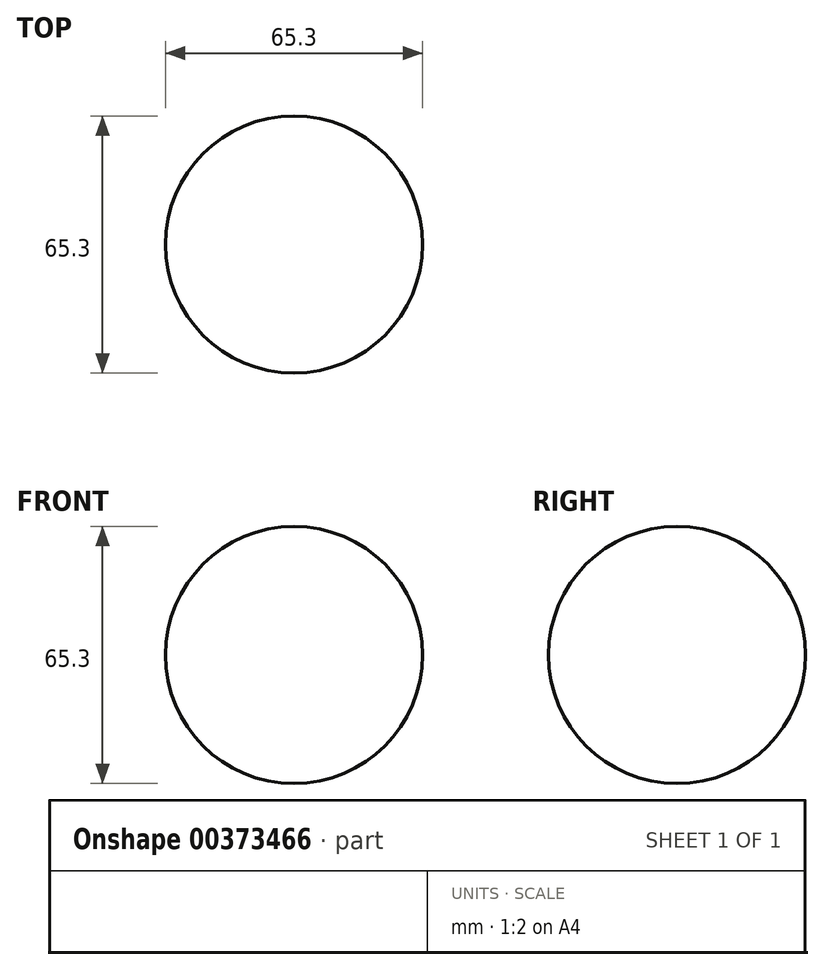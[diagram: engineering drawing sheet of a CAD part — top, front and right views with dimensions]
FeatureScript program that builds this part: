
annotation { "Feature Type Name" : "Feature", "Feature Type Description" : "" }
export const myFeature = defineFeature(function(context is Context, id is Id, definition is map)
    precondition{}
    {
        {
            var Q0;
            Q0=qCreatedBy(makeId("Front.planeOp"),FACE);
            var sketch = newSketch(context, id + "F0", { "sketchPlane" : qUnion([Q0])});
            skCircle(sketch, "E0", {"center": v(0, 0) * mm, "radius": 32.65 * mm});
            skLineSegment(sketch, "E1", {"start": v(0, 32.65) * mm, "end": v(0, -32.65) * mm});
            skSolve(sketch);
        }
        {
            var Q0;
            {var subQ0=sQuery(id+"F0.wireOp",EDGE,"E1");Q0=makeQuery(id+"F0.imprint","IMPRINT",FACE,{"disambiguationData":[TD([[makeQuery(id+"F0.imprint","IMPRINT",EDGE,{"derivedFrom":subQ0}),1.0]])]});}
            var Q1;
            Q1=sQuery(id+"F0.wireOp",EDGE,"E1");
            revolve(context, id + "F1", {"entities" : qUnion([Q0]), "axis" : qUnion([Q1]), "revolveType" : RevolveType.FULL});
        }
    });
